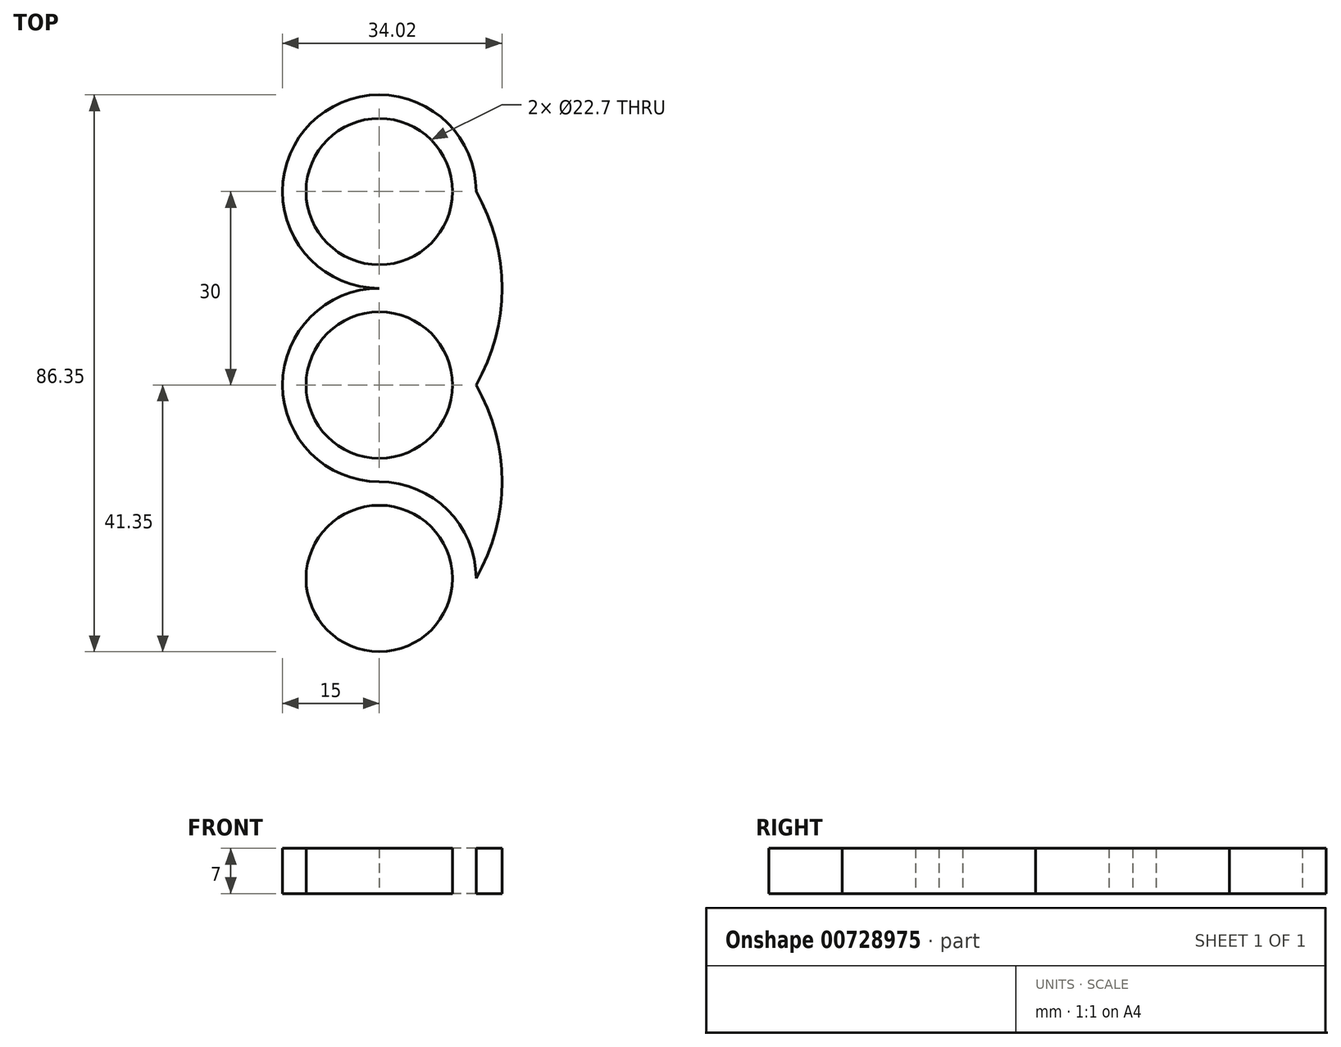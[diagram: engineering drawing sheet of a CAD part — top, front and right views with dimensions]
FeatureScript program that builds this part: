
annotation { "Feature Type Name" : "Feature", "Feature Type Description" : "" }
export const myFeature = defineFeature(function(context is Context, id is Id, definition is map)
    precondition{}
    {
        {
            var Q0;
            Q0=qCreatedBy(makeId("Top.planeOp"),FACE);
            var sketch = newSketch(context, id + "F0", { "sketchPlane" : qUnion([Q0])});
            skCircle(sketch, "E0", {"center": v(0, 0) * mm, "radius": 11.35 * mm});
            skCircle(sketch, "E1", {"center": v(0, 0) * mm, "radius": 15 * mm});
            skCircle(sketch, "E2", {"center": v(0, 30) * mm, "radius": 11.35 * mm});
            skCircle(sketch, "E3", {"center": v(0, 30) * mm, "radius": 15 * mm});
            skCircle(sketch, "E4.MirrorC", {"center": v(0, -30) * mm, "radius": 11.35 * mm});
            skCircle(sketch, "E5.MirrorC", {"center": v(0, -30) * mm, "radius": 15 * mm});
            skArc(sketch, "E6", {"start": v(15, 0) * mm, "mid": v(19.02, 15) * mm, "end": v(15, 30) * mm});
            skArc(sketch, "E7", {"start": v(15, -30) * mm, "mid": v(19.02, -15) * mm, "end": v(15, 0) * mm});
            skArc(sketch, "E8.MirrorCS", {"start": v(-15, 0) * mm, "mid": v(-19.02, 15) * mm, "end": v(-15, 30) * mm});
            skArc(sketch, "E9.MirrorCS", {"start": v(-15, -30) * mm, "mid": v(-19.02, -15) * mm, "end": v(-15, 0) * mm});
            skSolve(sketch);
        }
        {
            var Q0;
            {var subQ7=sQuery(id+"F0.wireOp",EDGE,"6d84073d-9e7e-4eba-87f3-d19ee50946a6.sketch_text.stroke-12");Q0=makeQuery(id+"F0.imprint","IMPRINT",FACE,{"disambiguationData":[TD([[makeQuery(id+"F0.imprint","IMPRINT",EDGE,{"derivedFrom":subQ7}),-1.0]])]});}
            var Q1;
            Q1=makeQuery(id+"F0.imprint","IMPRINT",FACE,{"disambiguationData":[TD([[makeQuery(id+"F0.imprint","IMPRINT",EDGE,{"derivedFrom":sQuery(id+"F0.wireOp",EDGE,"6d84073d-9e7e-4eba-87f3-d19ee50946a6.sketch_text.stroke-0")}),-1.0]])]});
            var Q2;
            {var subQ0=sQuery(id+"F0.wireOp",EDGE,"6d84073d-9e7e-4eba-87f3-d19ee50946a6.sketch_text.stroke-16");Q2=makeQuery(id+"F0.imprint","IMPRINT",FACE,{"disambiguationData":[TD([[makeQuery(id+"F0.imprint","IMPRINT",EDGE,{"derivedFrom":subQ0}),-1.0]])]});}
            var Q3;
            {var subQ7=sQuery(id+"F0.wireOp",EDGE,"E7CsGSGl-4yaB-JcIg-GimG-juy0E3IbdGsT");var subQ10=sQuery(id+"F0.wireOp",EDGE,"6d84073d-9e7e-4eba-87f3-d19ee50946a6.sketch_text.stroke-19");var subQ11=makeQuery(id+"F0.imprint","INTERSECT",VERTEX,{"derivedFrom":[subQ7,subQ10]});Q3=makeQuery(id+"F0.imprint","IMPRINT",FACE,{"disambiguationData":[TD([[makeQuery(id+"F0.imprint","IMPRINT",EDGE,{"disambiguationData":[TD([[subQ11,1.0]])],"derivedFrom":subQ7}),-1.0]])]});}
            var Q4;
            {var subQ0=sQuery(id+"F0.wireOp",EDGE,"6d84073d-9e7e-4eba-87f3-d19ee50946a6.sketch_text.stroke-17");var subQ1=sQuery(id+"F0.wireOp",EDGE,"E7CsGSGl-4yaB-JcIg-GimG-juy0E3IbdGsT");var subQ2=makeQuery(id+"F0.imprint","INTERSECT",VERTEX,{"derivedFrom":[subQ1,subQ0]});Q4=makeQuery(id+"F0.imprint","IMPRINT",FACE,{"disambiguationData":[TD([[makeQuery(id+"F0.imprint","IMPRINT",EDGE,{"disambiguationData":[TD([[subQ2,1.0]])],"derivedFrom":subQ1}),-1.0]])]});}
            var Q5;
            {var subQ0=sQuery(id+"F0.wireOp",EDGE,"6d84073d-9e7e-4eba-87f3-d19ee50946a6.sketch_text.stroke-19");var subQ1=sQuery(id+"F0.wireOp",EDGE,"E7CsGSGl-4yaB-JcIg-GimG-juy0E3IbdGsT");var subQ2=makeQuery(id+"F0.imprint","INTERSECT",VERTEX,{"derivedFrom":[subQ1,subQ0]});Q5=makeQuery(id+"F0.imprint","IMPRINT",FACE,{"disambiguationData":[TD([[makeQuery(id+"F0.imprint","IMPRINT",EDGE,{"disambiguationData":[TD([[subQ2,-1.0]])],"derivedFrom":subQ1}),-1.0]])]});}
            var Q6;
            {var subQ0=sQuery(id+"F0.wireOp",EDGE,"rSFXYw65-SHp5-DZoC-vZtT-DSTp1olF5W8k");var subQ1=sQuery(id+"F0.wireOp",EDGE,"E1");var subQ2=makeQuery(id+"F0.imprint","INTERSECT",VERTEX,{"disambiguationData":[OD(0.0)],"derivedFrom":[subQ1,subQ0]});Q6=makeQuery(id+"F0.imprint","IMPRINT",FACE,{"disambiguationData":[TD([[makeQuery(id+"F0.imprint","IMPRINT",EDGE,{"disambiguationData":[TD([[subQ2,-1.0]])],"derivedFrom":subQ1}),1.0]])]});}
            var Q7;
            {var subQ0=sQuery(id+"F0.wireOp",EDGE,"rSFXYw65-SHp5-DZoC-vZtT-DSTp1olF5W8k");var subQ1=sQuery(id+"F0.wireOp",EDGE,"E0");var subQ2=makeQuery(id+"F0.imprint","INTERSECT",VERTEX,{"derivedFrom":[subQ1,subQ0]});Q7=makeQuery(id+"F0.imprint","IMPRINT",FACE,{"disambiguationData":[TD([[makeQuery(id+"F0.imprint","IMPRINT",EDGE,{"disambiguationData":[TD([[subQ2,1.0]])],"derivedFrom":subQ1}),-1.0]])]});}
            var Q8;
            {var subQ3=sQuery(id+"F0.wireOp",EDGE,"rSFXYw65-SHp5-DZoC-vZtT-DSTp1olF5W8k");var subQ7=sQuery(id+"F0.wireOp",EDGE,"E0");var subQ9=makeQuery(id+"F0.imprint","INTERSECT",VERTEX,{"derivedFrom":[subQ7,subQ3]});Q8=makeQuery(id+"F0.imprint","IMPRINT",FACE,{"disambiguationData":[TD([[makeQuery(id+"F0.imprint","IMPRINT",EDGE,{"disambiguationData":[TD([[subQ9,-1.0]])],"derivedFrom":subQ7}),-1.0]])]});}
            var Q9;
            {var subQ0=sQuery(id+"F0.wireOp",EDGE,"6d84073d-9e7e-4eba-87f3-d19ee50946a6.sketch_text.stroke-22");var subQ3=sQuery(id+"F0.wireOp",EDGE,"E0");var subQ4=makeQuery(id+"F0.imprint","INTERSECT",VERTEX,{"derivedFrom":[subQ3,subQ0]});Q9=makeQuery(id+"F0.imprint","IMPRINT",FACE,{"disambiguationData":[TD([[makeQuery(id+"F0.imprint","IMPRINT",EDGE,{"disambiguationData":[TD([[subQ4,-1.0]])],"derivedFrom":subQ3}),-1.0]])]});}
            var Q10;
            {var subQ0=sQuery(id+"F0.wireOp",EDGE,"6d84073d-9e7e-4eba-87f3-d19ee50946a6.sketch_text.stroke-11");var subQ1=sQuery(id+"F0.wireOp",EDGE,"E0");var subQ2=makeQuery(id+"F0.imprint","INTERSECT",VERTEX,{"derivedFrom":[subQ1,subQ0]});Q10=makeQuery(id+"F0.imprint","IMPRINT",FACE,{"disambiguationData":[TD([[makeQuery(id+"F0.imprint","IMPRINT",EDGE,{"disambiguationData":[TD([[subQ2,-1.0]])],"derivedFrom":subQ1}),-1.0]])]});}
            var Q11;
            {var subQ0=sQuery(id+"F0.wireOp",EDGE,"CD1cir0j-4PbA-lUsg-vOLo-TSWTPvtZ9WnU");var subQ1=sQuery(id+"F0.wireOp",EDGE,"E1");var subQ2=makeQuery(id+"F0.imprint","INTERSECT",VERTEX,{"disambiguationData":[OD(0.0)],"derivedFrom":[subQ1,subQ0]});Q11=makeQuery(id+"F0.imprint","IMPRINT",FACE,{"disambiguationData":[TD([[makeQuery(id+"F0.imprint","IMPRINT",EDGE,{"disambiguationData":[TD([[subQ2,-1.0]])],"derivedFrom":subQ1}),1.0]])]});}
            var Q12;
            {var subQ0=sQuery(id+"F0.wireOp",EDGE,"CD1cir0j-4PbA-lUsg-vOLo-TSWTPvtZ9WnU");var subQ1=sQuery(id+"F0.wireOp",EDGE,"E0");var subQ2=makeQuery(id+"F0.imprint","INTERSECT",VERTEX,{"derivedFrom":[subQ1,subQ0]});Q12=makeQuery(id+"F0.imprint","IMPRINT",FACE,{"disambiguationData":[TD([[makeQuery(id+"F0.imprint","IMPRINT",EDGE,{"disambiguationData":[TD([[subQ2,-1.0]])],"derivedFrom":subQ1}),-1.0]])]});}
            var Q13;
            {var subQ0=sQuery(id+"F0.wireOp",EDGE,"6d84073d-9e7e-4eba-87f3-d19ee50946a6.sketch_text.stroke-23");var subQ1=sQuery(id+"F0.wireOp",EDGE,"E0");var subQ2=makeQuery(id+"F0.imprint","INTERSECT",VERTEX,{"derivedFrom":[subQ1,subQ0]});Q13=makeQuery(id+"F0.imprint","IMPRINT",FACE,{"disambiguationData":[TD([[makeQuery(id+"F0.imprint","IMPRINT",EDGE,{"disambiguationData":[TD([[subQ2,1.0]])],"derivedFrom":subQ1}),-1.0]])]});}
            var Q14;
            {var subQ4=sQuery(id+"F0.wireOp",EDGE,"6d84073d-9e7e-4eba-87f3-d19ee50946a6.sketch_text.stroke-3");Q14=makeQuery(id+"F0.imprint","IMPRINT",FACE,{"disambiguationData":[TD([[makeQuery(id+"F0.imprint","IMPRINT",EDGE,{"derivedFrom":subQ4}),-1.0]])]});}
            var Q15;
            {var subQ1=sQuery(id+"F0.wireOp",EDGE,"6d84073d-9e7e-4eba-87f3-d19ee50946a6.sketch_text.stroke-5");var subQ3=sQuery(id+"F0.wireOp",EDGE,"3b3fd6d6-9819-4dca-a65f-230b90d0e1ed0.MirrorC");var subQ4=makeQuery(id+"F0.imprint","INTERSECT",VERTEX,{"derivedFrom":[subQ3,subQ1]});Q15=makeQuery(id+"F0.imprint","IMPRINT",FACE,{"disambiguationData":[TD([[makeQuery(id+"F0.imprint","IMPRINT",EDGE,{"disambiguationData":[TD([[subQ4,1.0]])],"derivedFrom":subQ3}),1.0]])]});}
            var Q16;
            {var subQ0=sQuery(id+"F0.wireOp",EDGE,"6d84073d-9e7e-4eba-87f3-d19ee50946a6.sketch_text.stroke-5");var subQ1=sQuery(id+"F0.wireOp",EDGE,"3b3fd6d6-9819-4dca-a65f-230b90d0e1ed0.MirrorC");var subQ2=makeQuery(id+"F0.imprint","INTERSECT",VERTEX,{"derivedFrom":[subQ1,subQ0]});Q16=makeQuery(id+"F0.imprint","IMPRINT",FACE,{"disambiguationData":[TD([[makeQuery(id+"F0.imprint","IMPRINT",EDGE,{"disambiguationData":[TD([[subQ2,-1.0]])],"derivedFrom":subQ1}),1.0]])]});}
            var Q17;
            {var subQ0=sQuery(id+"F0.wireOp",EDGE,"6d84073d-9e7e-4eba-87f3-d19ee50946a6.sketch_text.stroke-7");var subQ1=sQuery(id+"F0.wireOp",EDGE,"3b3fd6d6-9819-4dca-a65f-230b90d0e1ed0.MirrorC");var subQ2=makeQuery(id+"F0.imprint","INTERSECT",VERTEX,{"derivedFrom":[subQ1,subQ0]});Q17=makeQuery(id+"F0.imprint","IMPRINT",FACE,{"disambiguationData":[TD([[makeQuery(id+"F0.imprint","IMPRINT",EDGE,{"disambiguationData":[TD([[subQ2,1.0]])],"derivedFrom":subQ1}),1.0]])]});}
            var Q18;
            {var subQ0=sQuery(id+"F0.wireOp",EDGE,"6d84073d-9e7e-4eba-87f3-d19ee50946a6.sketch_text.stroke-15");var subQ1=sQuery(id+"F0.wireOp",EDGE,"6d84073d-9e7e-4eba-87f3-d19ee50946a6.sketch_text.stroke-14");var subQ2=makeQuery(id+"F0.imprint","INTERSECT",VERTEX,{"derivedFrom":[subQ1,subQ0]});Q18=makeQuery(id+"F0.imprint","IMPRINT",FACE,{"disambiguationData":[TD([[makeQuery(id+"F0.imprint","IMPRINT",EDGE,{"disambiguationData":[TD([[subQ2,1.0]])],"derivedFrom":subQ1}),1.0]])]});}
            var Q19;
            {var subQ0=sQuery(id+"F0.wireOp",EDGE,"6d84073d-9e7e-4eba-87f3-d19ee50946a6.sketch_text.stroke-2");var subQ1=sQuery(id+"F0.wireOp",EDGE,"6d84073d-9e7e-4eba-87f3-d19ee50946a6.sketch_text.stroke-1");var subQ2=makeQuery(id+"F0.imprint","INTERSECT",VERTEX,{"derivedFrom":[subQ1,subQ0]});Q19=makeQuery(id+"F0.imprint","IMPRINT",FACE,{"disambiguationData":[TD([[makeQuery(id+"F0.imprint","IMPRINT",EDGE,{"disambiguationData":[TD([[subQ2,1.0]])],"derivedFrom":subQ1}),1.0]])]});}
            var Q20;
            {var subQ0=sQuery(id+"F0.wireOp",EDGE,"KyivtgkW-Nr9b-VoJL-LyPU-W7SQRqYEa32X");Q20=makeQuery(id+"F0.imprint","IMPRINT",FACE,{"disambiguationData":[TD([[makeQuery(id+"F0.imprint","IMPRINT",EDGE,{"derivedFrom":subQ0}),1.0]])]});}
            var Q21;
            {var subQ1=sQuery(id+"F0.wireOp",EDGE,"E1");var subQ3=makeQuery(id+"F0.imprint","INTERSECT",VERTEX,{"derivedFrom":[sQuery(id+"F0.wireOp",EDGE,"3b3fd6d6-9819-4dca-a65f-230b90d0e1ed0.MirrorC"),subQ1]});Q21=makeQuery(id+"F0.imprint","IMPRINT",FACE,{"disambiguationData":[TD([[makeQuery(id+"F0.imprint","IMPRINT",EDGE,{"disambiguationData":[TD([[subQ3,-1.0]])],"derivedFrom":subQ1}),1.0]])]});}
            var Q22;
            {var subQ1=sQuery(id+"F0.wireOp",EDGE,"E1");var subQ3=makeQuery(id+"F0.imprint","INTERSECT",VERTEX,{"derivedFrom":[sQuery(id+"F0.wireOp",EDGE,"E7CsGSGl-4yaB-JcIg-GimG-juy0E3IbdGsT"),subQ1]});Q22=makeQuery(id+"F0.imprint","IMPRINT",FACE,{"disambiguationData":[TD([[makeQuery(id+"F0.imprint","IMPRINT",EDGE,{"disambiguationData":[TD([[subQ3,-1.0]])],"derivedFrom":subQ1}),1.0]])]});}
            var Q23;
            {var subQ0=sQuery(id+"F0.wireOp",EDGE,"82a913d8-ce4d-4fd3-9c12-226740bcec2d0.MirrorCS");Q23=makeQuery(id+"F0.imprint","IMPRINT",FACE,{"disambiguationData":[TD([[makeQuery(id+"F0.imprint","IMPRINT",EDGE,{"derivedFrom":subQ0}),1.0]])]});}
            var Q24;
            {var subQ0=sQuery(id+"F0.wireOp",EDGE,"0bcd2ed7-4bd2-424b-b183-8a66f11eee9f0.MirrorCS");Q24=makeQuery(id+"F0.imprint","IMPRINT",FACE,{"disambiguationData":[TD([[makeQuery(id+"F0.imprint","IMPRINT",EDGE,{"derivedFrom":subQ0}),1.0]])]});}
            var Q25;
            {var subQ0=sQuery(id+"F0.wireOp",EDGE,"LALpeLYK-kdxA-iaYw-iG5N-8gkLFXYcywny");Q25=makeQuery(id+"F0.imprint","IMPRINT",FACE,{"disambiguationData":[TD([[makeQuery(id+"F0.imprint","IMPRINT",EDGE,{"derivedFrom":subQ0}),-1.0]])]});}
            var Q26;
            {var subQ0=sQuery(id+"F0.wireOp",EDGE,"E8.MirrorCS");Q26=makeQuery(id+"F0.imprint","IMPRINT",FACE,{"disambiguationData":[TD([[makeQuery(id+"F0.imprint","IMPRINT",EDGE,{"derivedFrom":subQ0}),-1.0]])]});}
            var Q27;
            Q27=makeQuery(id+"F0.imprint","IMPRINT",FACE,{"disambiguationData":[TD([[makeQuery(id+"F0.imprint","IMPRINT",EDGE,{"derivedFrom":sQuery(id+"F0.wireOp",EDGE,"E2")}),-1.0]])]});
            var Q28;
            {var subQ0=sQuery(id+"F0.wireOp",EDGE,"E6");Q28=makeQuery(id+"F0.imprint","IMPRINT",FACE,{"disambiguationData":[TD([[makeQuery(id+"F0.imprint","IMPRINT",EDGE,{"derivedFrom":subQ0}),1.0]])]});}
            var Q29;
            {var subQ0=sQuery(id+"F0.wireOp",EDGE,"E7");Q29=makeQuery(id+"F0.imprint","IMPRINT",FACE,{"disambiguationData":[TD([[makeQuery(id+"F0.imprint","IMPRINT",EDGE,{"derivedFrom":subQ0}),1.0]])]});}
            var Q30;
            {var subQ0=sQuery(id+"F0.wireOp",EDGE,"E9.MirrorCS");Q30=makeQuery(id+"F0.imprint","IMPRINT",FACE,{"disambiguationData":[TD([[makeQuery(id+"F0.imprint","IMPRINT",EDGE,{"derivedFrom":subQ0}),-1.0]])]});}
            var Q31;
            Q31=makeQuery(id+"F0.imprint","IMPRINT",FACE,{"disambiguationData":[TD([[makeQuery(id+"F0.imprint","IMPRINT",EDGE,{"derivedFrom":sQuery(id+"F0.wireOp",EDGE,"E4.MirrorC")}),1.0]])]});
            extrude(context, id + "F1", {"entities" : qUnion([Q0, Q1, Q2, Q3, Q4, Q5, Q6, Q7, Q8, Q9, Q10, Q11, Q12, Q13, Q14, Q15, Q16, Q17, Q18, Q19, Q20, Q21, Q22, Q23, Q24, Q25, Q26, Q27, Q28, Q29, Q30, Q31]), "depth" : 7 * mm, "offsetDistance" : 25 * mm});
        }
    });
